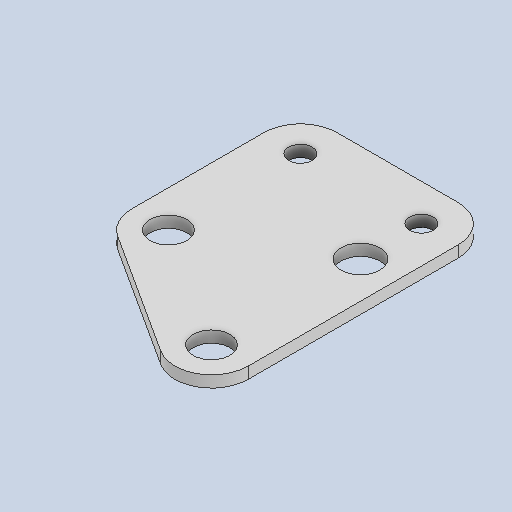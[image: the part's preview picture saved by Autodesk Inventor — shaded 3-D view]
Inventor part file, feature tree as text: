
AUTODESK INVENTOR PART (.ipt)
format: ipt  version: 2024.2 (Build 282272000, 272)  size: 98,304 bytes
history: native  units: in
note: dims shown in document units (in); Inventor stores cm internally (conversion verified against a paired STEP export)
features: fillet x1
ambient origin geometry x8: Origin, YZ Plane, XZ Plane, XY Plane, X Axis, Y Axis, Z Axis, Center Point
bodies: Solid1 (feature_tree)
feature tree (1):
  fillet  "Fillet1"  [1 undecoded]
note: 1 required parameter value undecoded (feature->parameter linkage not recoverable at this tier; creation-order binding heuristic only, values carry confidence <= 0.55)
